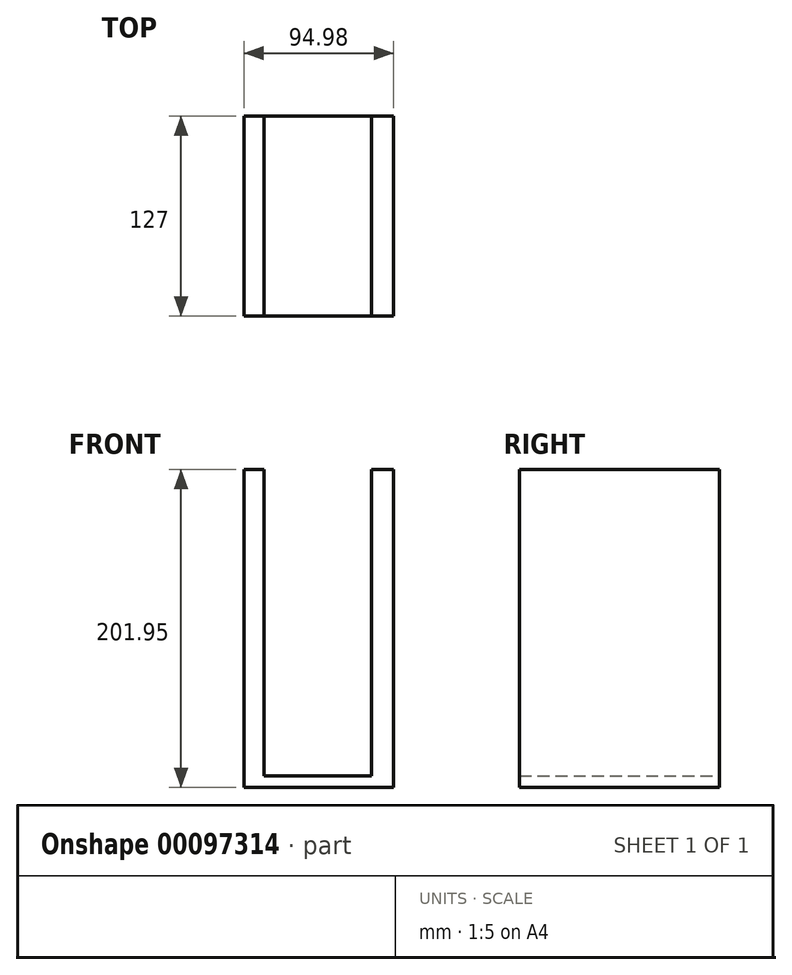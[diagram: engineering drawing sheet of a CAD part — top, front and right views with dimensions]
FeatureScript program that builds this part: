
annotation { "Feature Type Name" : "Feature", "Feature Type Description" : "" }
export const myFeature = defineFeature(function(context is Context, id is Id, definition is map)
    precondition{}
    {
        {
            var Q0;
            Q0=qCreatedBy(makeId("Front.planeOp"),FACE);
            var sketch = newSketch(context, id + "F0", { "sketchPlane" : qUnion([Q0])});
            skLineSegment(sketch, "E0.bottom", {"start": v(-44.78, 93.13) * mm, "end": v(50.2, 93.13) * mm});
            skLineSegment(sketch, "E0.top", {"start": v(-44.78, -108.82) * mm, "end": v(50.2, -108.82) * mm});
            skLineSegment(sketch, "E0.left", {"start": v(-44.78, 93.13) * mm, "end": v(-44.78, -108.82) * mm});
            skLineSegment(sketch, "E0.right", {"start": v(50.2, 93.13) * mm, "end": v(50.2, -108.82) * mm});
            skLineSegment(sketch, "E1.bottom", {"start": v(-32.06, 114.62) * mm, "end": v(36.24, 114.62) * mm});
            skLineSegment(sketch, "E1.top", {"start": v(-32.06, -101.4) * mm, "end": v(36.24, -101.4) * mm});
            skLineSegment(sketch, "E1.left", {"start": v(-32.06, 114.62) * mm, "end": v(-32.06, -101.4) * mm});
            skLineSegment(sketch, "E1.right", {"start": v(36.24, 114.62) * mm, "end": v(36.24, -101.4) * mm});
            skSolve(sketch);
        }
        {
            var Q0;
            Q0=makeQuery(id+"F0.imprint","IMPRINT",FACE,{"disambiguationData":[TD([[makeQuery(id+"F0.imprint","IMPRINT",EDGE,{"derivedFrom":sQuery(id+"F0.wireOp",EDGE,"E0.bottom")}),-1.0]])]});
            extrude(context, id + "F1", {"entities" : qUnion([Q0]), "depth" : 127 * mm});
        }
    });
